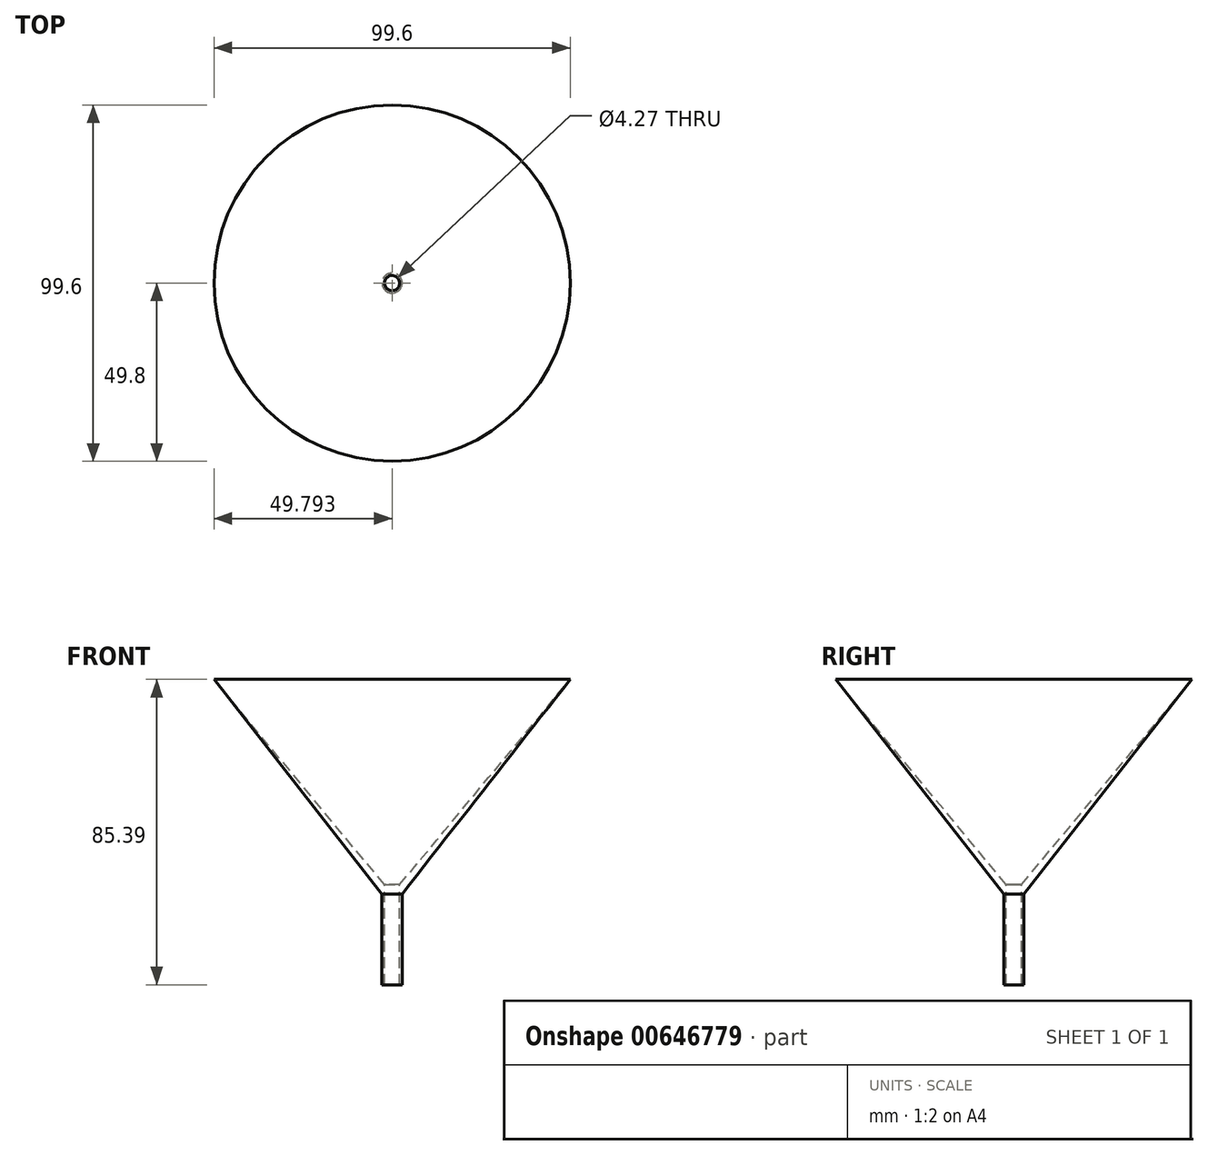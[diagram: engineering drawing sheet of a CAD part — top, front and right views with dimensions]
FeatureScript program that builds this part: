
annotation { "Feature Type Name" : "Feature", "Feature Type Description" : "" }
export const myFeature = defineFeature(function(context is Context, id is Id, definition is map)
    precondition{}
    {
        {
            var Q0;
            Q0=qCreatedBy(makeId("Front.planeOp"),FACE);
            var sketch = newSketch(context, id + "F0", { "sketchPlane" : qUnion([Q0])});
            skLineSegment(sketch, "E0", {"start": v(0, -51.64) * mm, "end": v(0, -26.24) * mm});
            skLineSegment(sketch, "E1", {"start": v(0, -26.24) * mm, "end": v(46.98, 33.75) * mm});
            skLineSegment(sketch, "E2", {"start": v(46.98, 33.75) * mm, "end": v(-2.82, -26.24) * mm});
            skLineSegment(sketch, "E3", {"start": v(-2.82, -26.24) * mm, "end": v(-2.82, -51.44) * mm});
            skLineSegment(sketch, "E4", {"start": v(-2.82, -51.44) * mm, "end": v(0, -51.64) * mm});
            skSolve(sketch);
        }
        {
            var Q0;
            Q0=makeQuery(id+"F0.imprint","IMPRINT",FACE,{"disambiguationData":[TD([[makeQuery(id+"F0.imprint","IMPRINT",EDGE,{"derivedFrom":sQuery(id+"F0.wireOp",EDGE,"E0")}),1.0]])]});
            var Q1;
            Q1=sQuery(id+"F0.wireOp",EDGE,"E3");
            revolve(context, id + "F1", {"entities" : qUnion([Q0]), "axis" : qUnion([Q1]), "revolveType" : RevolveType.FULL});
        }
        {
            var Q0;
            Q0=qCreatedBy(makeId("Top.planeOp"),FACE);
            var sketch = newSketch(context, id + "F2", { "sketchPlane" : qUnion([Q0])});
            skCircle(sketch, "E5", {"center": v(-2.83, 0) * mm, "radius": 2.14 * mm});
            skSolve(sketch);
        }
        {
            var Q0;
            Q0 = qSketchRegion(id + "F2", true);
            extrude(context, id + "F3", {"entities" : qUnion([Q0]), "operationType" : NewBodyOperationType.REMOVE, "oppositeDirection" : true, "depth" : 65.8 * mm, "offsetDistance" : 25.4 * mm});
        }
    });
